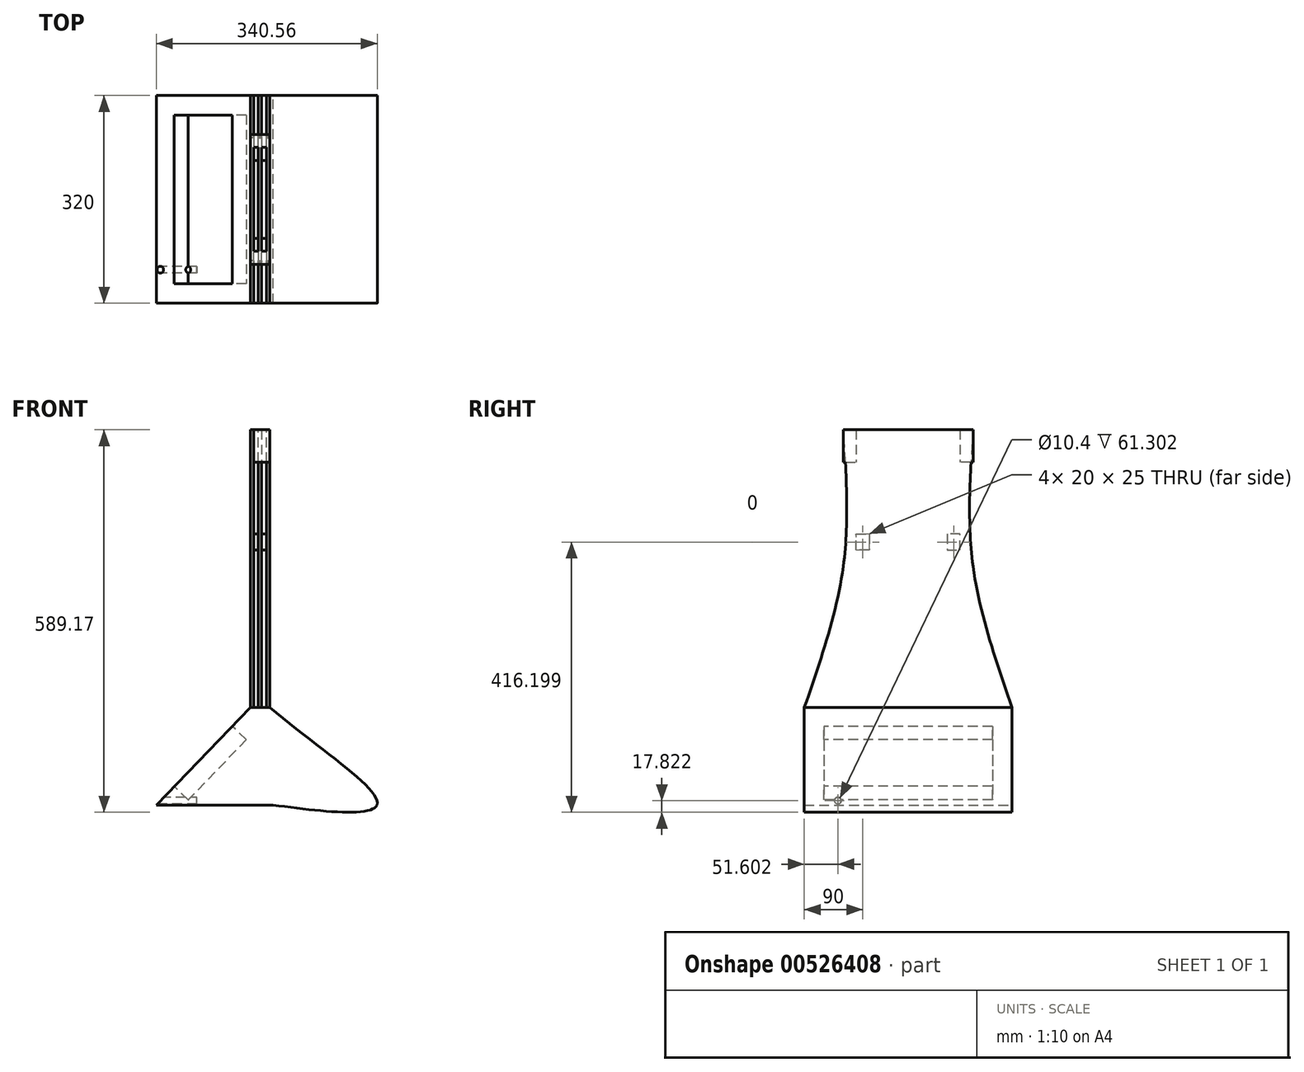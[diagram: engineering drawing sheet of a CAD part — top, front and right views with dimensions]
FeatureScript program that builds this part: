
annotation { "Feature Type Name" : "Feature", "Feature Type Description" : "" }
export const myFeature = defineFeature(function(context is Context, id is Id, definition is map)
    precondition{}
    {
        {
            var Q0;
            Q0=qCreatedBy(makeId("Front.planeOp"),FACE);
            var sketch = newSketch(context, id + "F0", { "sketchPlane" : qUnion([Q0])});
            skFitSpline(sketch, "E0", {"points": [v(180.3, 1.14) * mm, v(340.3, 1.14) * mm, v(175.3, 151.14) * mm], "startDerivative": vector(446.66, -62.32) * mm, "endDerivative": vector(-420, 349.65) * mm});
            skLineSegment(sketch, "E1", {"start": v(180.3, 1.14) * mm, "end": v(340.3, 1.14) * mm});
            skLineSegment(sketch, "E2", {"start": v(175.3, 151.14) * mm, "end": v(145.3, 151.14) * mm});
            skLineSegment(sketch, "E3", {"start": v(150.3, 1.14) * mm, "end": v(180.3, 1.14) * mm});
            skLineSegment(sketch, "E4", {"start": v(150.3, 1.14) * mm, "end": v(100.3, 1.14) * mm});
            skLineSegment(sketch, "E5", {"start": v(100.3, 1.14) * mm, "end": v(0.3, 1.14) * mm});
            skLineSegment(sketch, "E6", {"start": v(0.3, 1.14) * mm, "end": v(145.3, 151.14) * mm});
            skSolve(sketch);
        }
        {
            var Q0;
            Q0=qSketchRegion(id+"F0",true);
            extrude(context, id + "F1", {"entities" : qUnion([Q0]), "depth" : 320 * mm, "offsetDistance" : 25 * mm});
        }
        {
            var Q0;
            Q0=makeQuery(id+"F1.opExtrude","SWEPT_FACE",FACE,{"disambiguationData":[OSD([sQuery(id+"F0.wireOp",EDGE,"E2")])]});
            var sketch = newSketch(context, id + "F2", { "sketchPlane" : qUnion([Q0])});
            skLineSegment(sketch, "E7", {"start": v(145.3, 0) * mm, "end": v(175.3, 0) * mm});
            skLineSegment(sketch, "E8", {"start": v(175.3, 0) * mm, "end": v(175.3, -320) * mm});
            skLineSegment(sketch, "E9", {"start": v(175.3, -320) * mm, "end": v(145.3, -320) * mm});
            skLineSegment(sketch, "E10", {"start": v(145.3, -320) * mm, "end": v(145.3, 0) * mm});
            skSolve(sketch);
        }
        {
            var Q0;
            Q0=qSketchRegion(id+"F2",true);
            extrude(context, id + "F3", {"entities" : qUnion([Q0]), "operationType" : NewBodyOperationType.ADD, "depth" : 428 * mm, "offsetDistance" : 25 * mm});
        }
        {
            var Q0;
            Q0=makeQuery(id+"F3.opExtrude","SWEPT_FACE",FACE,{"disambiguationData":[OSD([sQuery(id+"F2.wireOp",EDGE,"E10")])]});
            var sketch = newSketch(context, id + "F4", { "sketchPlane" : qUnion([Q0])});
            skLineSegment(sketch, "E11", {"start": v(0, 151.14) * mm, "end": v(0, 579.14) * mm});
            skLineSegment(sketch, "E12", {"start": v(0, 579.14) * mm, "end": v(60, 579.14) * mm});
            skLineSegment(sketch, "E13", {"start": v(320, 151.14) * mm, "end": v(320, 579.14) * mm});
            skLineSegment(sketch, "E14", {"start": v(320, 579.14) * mm, "end": v(260, 579.14) * mm});
            skFitSpline(sketch, "E15", {"points": [v(60, 579.14) * mm, v(60, 368.67) * mm, v(0, 151.14) * mm], "startDerivative": vector(28.97, -428.6) * mm, "endDerivative": vector(-147.95, -427.4) * mm});
            skFitSpline(sketch, "E16", {"points": [v(320, 151.14) * mm, v(260, 368.67) * mm, v(260, 579.14) * mm], "startDerivative": vector(-147.95, 427.4) * mm, "endDerivative": vector(28.97, 428.6) * mm});
            skLineSegment(sketch, "E17", {"start": v(60, 368.67) * mm, "end": v(60, 579.14) * mm});
            skLineSegment(sketch, "E18", {"start": v(260, 368.67) * mm, "end": v(260, 579.14) * mm});
            skPoint(sketch, "E19.centerSnap0", {"position": v(160, 579.14) * mm});
            skLineSegment(sketch, "E20", {"start": v(260, 579.14) * mm, "end": v(230, 579.14) * mm});
            skPoint(sketch, "E21.end.orphan", {"position": v(260, 508.95) * mm});
            skPoint(sketch, "E22.centerSnap0", {"position": v(230, 544.14) * mm});
            skPoint(sketch, "E22.centerSnap1", {"position": v(245, 579.14) * mm});
            skPoint(sketch, "E23.orphan", {"position": v(230, 509.14) * mm});
            skLineSegment(sketch, "E24", {"start": v(60, 579.14) * mm, "end": v(90, 579.14) * mm});
            skPoint(sketch, "E25.centerSnap0", {"position": v(75, 579.14) * mm});
            skPoint(sketch, "E19.center.orphan", {"position": v(160, 387.68) * mm});
            skPoint(sketch, "E25.center.orphan", {"position": v(75, 559.14) * mm});
            skPoint(sketch, "E26.center.orphan", {"position": v(75, 529.14) * mm});
            skPoint(sketch, "E27.center.orphan", {"position": v(245, 559.14) * mm});
            skPoint(sketch, "E28.center.orphan", {"position": v(245, 529.14) * mm});
            skPoint(sketch, "E29.center.orphan", {"position": v(160, 357.68) * mm});
            skSolve(sketch);
        }
        {
            var Q0;
            Q0=qSketchRegion(id+"F4",true);
            extrude(context, id + "F5", {"entities" : qUnion([Q0]), "operationType" : NewBodyOperationType.REMOVE, "oppositeDirection" : true, "depth" : 205 * mm, "offsetDistance" : 25 * mm});
        }
        {
            var Q0;
            Q0=makeQuery(id+"F3.opExtrude","SWEPT_FACE",FACE,{"disambiguationData":[OSD([sQuery(id+"F2.wireOp",EDGE,"E8")])]});
            var sketch = newSketch(context, id + "F6", { "sketchPlane" : qUnion([Q0])});
            skLineSegment(sketch, "E30.bottom", {"start": v(-260, 579.14) * mm, "end": v(-240, 579.14) * mm});
            skLineSegment(sketch, "E30.top", {"start": v(-260, 529.14) * mm, "end": v(-240, 529.14) * mm});
            skLineSegment(sketch, "E30.left", {"start": v(-260, 579.14) * mm, "end": v(-260, 529.14) * mm});
            skLineSegment(sketch, "E30.right", {"start": v(-240, 579.14) * mm, "end": v(-240, 529.14) * mm});
            skLineSegment(sketch, "E31.bottom", {"start": v(-60, 579.14) * mm, "end": v(-80, 579.14) * mm});
            skLineSegment(sketch, "E31.top", {"start": v(-60, 529.14) * mm, "end": v(-80, 529.14) * mm});
            skLineSegment(sketch, "E31.left", {"start": v(-60, 579.14) * mm, "end": v(-60, 529.14) * mm});
            skLineSegment(sketch, "E31.right", {"start": v(-80, 579.14) * mm, "end": v(-80, 529.14) * mm});
            skLineSegment(sketch, "E32.right", {"start": v(-240, 393.67) * mm, "end": v(-240, 418.67) * mm});
            skLineSegment(sketch, "E33.right", {"start": v(-80, 393.67) * mm, "end": v(-80, 418.67) * mm});
            skPoint(sketch, "E32.bottom.end.orphan", {"position": v(-240, 368.67) * mm});
            skPoint(sketch, "E34.orphan", {"position": v(-260, 368.67) * mm});
            skPoint(sketch, "E33.bottom.end.orphan", {"position": v(-80, 368.67) * mm});
            skPoint(sketch, "E33.bottom.start.orphan", {"position": v(-60, 368.67) * mm});
            skLineSegment(sketch, "E35", {"start": v(-240, 418.67) * mm, "end": v(-220, 418.67) * mm});
            skLineSegment(sketch, "E36", {"start": v(-220, 418.67) * mm, "end": v(-220, 393.67) * mm});
            skLineSegment(sketch, "E37", {"start": v(-220, 393.67) * mm, "end": v(-240, 393.67) * mm});
            skPoint(sketch, "E32.left.end.orphan", {"position": v(-260, 418.67) * mm});
            skPoint(sketch, "E38.end.orphan", {"position": v(-260, 393.67) * mm});
            skLineSegment(sketch, "E39", {"start": v(-80, 418.67) * mm, "end": v(-100, 418.67) * mm});
            skLineSegment(sketch, "E40", {"start": v(-100, 418.67) * mm, "end": v(-100, 393.67) * mm});
            skLineSegment(sketch, "E41", {"start": v(-100, 393.67) * mm, "end": v(-80, 393.67) * mm});
            skPoint(sketch, "E33.left.end.orphan", {"position": v(-60, 418.67) * mm});
            skPoint(sketch, "E33.left.start.orphan", {"position": v(-60, 393.67) * mm});
            skSolve(sketch);
        }
        {
            var Q0;
            Q0=makeQuery(id+"F1.opExtrude","SWEPT_FACE",FACE,{"disambiguationData":[OSD([sQuery(id+"F0.wireOp",EDGE,"E6")])]});
            var sketch = newSketch(context, id + "F7", { "sketchPlane" : qUnion([Q0])});
            skLineSegment(sketch, "E42.bottom", {"start": v(30, 169.66) * mm, "end": v(290, 169.66) * mm});
            skLineSegment(sketch, "E42.top", {"start": v(30, 41.03) * mm, "end": v(290, 41.03) * mm});
            skLineSegment(sketch, "E42.left", {"start": v(30, 169.66) * mm, "end": v(30, 41.03) * mm});
            skLineSegment(sketch, "E42.right", {"start": v(290, 169.66) * mm, "end": v(290, 41.03) * mm});
            skSolve(sketch);
        }
        {
            var Q0;
            Q0=qSketchRegion(id+"F7",true);
            extrude(context, id + "F8", {"entities" : qUnion([Q0]), "operationType" : NewBodyOperationType.REMOVE, "oppositeDirection" : true, "depth" : 30 * mm, "offsetDistance" : 25 * mm});
        }
        {
            var Q0;
            Q0=makeQuery(id+"F3.boolean.opBoolean","MERGE",FACE,{"derivedFrom":[makeQuery(id+"F1.opExtrude","CAP_FACE",FACE,{"disambiguationData":[OSD([sQuery(id+"F0.wireOp",EDGE,"E0"),sQuery(id+"F0.wireOp",EDGE,"E1"),sQuery(id+"F0.wireOp",EDGE,"E2"),sQuery(id+"F0.wireOp",EDGE,"E3"),sQuery(id+"F0.wireOp",EDGE,"E4"),sQuery(id+"F0.wireOp",EDGE,"E5"),sQuery(id+"F0.wireOp",EDGE,"E6")])],"isStart":false}),makeQuery(id+"F3.opExtrude","SWEPT_FACE",FACE,{"disambiguationData":[OSD([sQuery(id+"F2.wireOp",EDGE,"E9")])]})]});
            var sketch = newSketch(context, id + "F9", { "sketchPlane" : qUnion([Q0])});
            skLineSegment(sketch, "E43", {"start": v(145.3, 151.14) * mm, "end": v(175.3, 151.14) * mm});
            skLineSegment(sketch, "E44", {"start": v(150.3, 151.14) * mm, "end": v(157.8, 151.14) * mm});
            skLineSegment(sketch, "E45", {"start": v(170.3, 151.14) * mm, "end": v(162.8, 151.14) * mm});
            skLineSegment(sketch, "E46", {"start": v(150.3, 151.14) * mm, "end": v(150.3, 608.36) * mm});
            skLineSegment(sketch, "E47", {"start": v(150.3, 608.36) * mm, "end": v(157.8, 608.36) * mm});
            skLineSegment(sketch, "E48", {"start": v(157.8, 608.36) * mm, "end": v(157.8, 151.14) * mm});
            skLineSegment(sketch, "E49", {"start": v(162.8, 151.14) * mm, "end": v(162.8, 608.36) * mm});
            skLineSegment(sketch, "E50", {"start": v(162.8, 608.36) * mm, "end": v(170.3, 608.36) * mm});
            skLineSegment(sketch, "E51", {"start": v(170.3, 608.36) * mm, "end": v(170.3, 151.14) * mm});
            skSolve(sketch);
        }
        {
            var Q0;
            Q0=qSketchRegion(id+"F9",true);
            extrude(context, id + "F10", {"entities" : qUnion([Q0]), "operationType" : NewBodyOperationType.REMOVE, "oppositeDirection" : true, "depth" : 977 * mm, "offsetDistance" : 25 * mm});
        }
        {
            var Q0;
            Q0=qSketchRegion(id+"F6",true);
            extrude(context, id + "F11", {"entities" : qUnion([Q0]), "operationType" : NewBodyOperationType.ADD, "oppositeDirection" : true, "depth" : 25 * mm, "offsetDistance" : 25 * mm});
        }
        {
            var Q0;
            Q0=qCreatedBy(makeId("Right.planeOp"),FACE);
            var sketch = newSketch(context, id + "F12", { "sketchPlane" : qUnion([Q0])});
            skCircle(sketch, "E52", {"center": v(-268.4, 7.8) * mm, "radius": 5.2 * mm});
            skSolve(sketch);
        }
        {
            var Q0;
            Q0=qSketchRegion(id+"F12",true);
            extrude(context, id + "F13", {"entities" : qUnion([Q0]), "operationType" : NewBodyOperationType.REMOVE, "depth" : 63 * mm, "offsetDistance" : 25 * mm});
        }
    });
